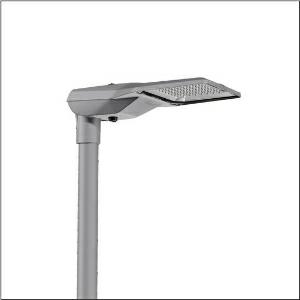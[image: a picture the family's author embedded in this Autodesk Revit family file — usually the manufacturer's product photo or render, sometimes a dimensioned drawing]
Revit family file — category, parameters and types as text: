
# Revit family: streetlight_sl_21_midi___st1_0a_5xe3d63t08lb_b124
name_source: partatom
category: Lighting Fixtures
units: mm (PartAtom-declared; Revit-internal decimal feet)

## family parameters
Cut with Voids When Loaded = No
Host = Face
Light Source = No
Part Type = Normal
Room Calculation Point = No
Round Connector Dimension = Use Diameter
Shared = No

## types (1)
- --- (1 x LED, 12860 lm, 99.6 W, 2700K)
    Apparent Load = 100 VA
    CIE Flux Codes = 37 72 97 100 100
    Color Rendering = 70
    Color Temperature = 2700K
    Default Elevation = 1800 mm
    Description = Streetlight SL 21 midi, mast luminaire, primary light control with lens, of PMMA, primary optical cover: cover, of toughened safety glass, transparent, light distribution: ST1.0a, light emission: direct distribution, primary light characteristic: asymmetric, installation type: side-entry, post-top, LED, High Power LED, rated luminous flux: 12.860lm, luminous efficacy: 129lm/W, light colour: 727, colour temperature: 2700K, control gear: D4i, control: overheat protection, constant luminous flux control, time-dependent luminous flux control, flexible luminous flux parameterisation, pre-setting: logarithmic dimming characteristic, mains connection: 230..240V, AC, 50/60Hz, start of lifetime: 100W, end of service life: 102W, reduction: 45W, luminaire housing, of diecast aluminium, powder-coated, SITECO metallic grey (DB 702S), corrosivity category C5 high according to DIN EN ISO 12944, please order mast flange separately, inclination adjustable: 0°, 5°, 10°, 15°, sealing non-destructively replaceable, multi-level sealing system, length: 644mm, width: 335mm, height: 110mm, mast flange for spigot size: 42mm (side-entry): 5XC10008XM4, 60/48mm (side-entry/post-top): 5XC10108XM2, 76/60mm (side-entry/post-top): 5XC10108XM1, mounting height: 4..8m, Smart Interface below and above, protection rating (complete): IP66, insulation class (complete): insulation class II (safety insulation), certification: CE, ENEC, ENEC+, VDE, impact resistance: IK10, permissible operating ambient temperature for outdoor applications: -40..+50°C, standard-compliant lighting for roads and squares, packaging unit: 1 piece

Light Distribution: ST1.0a
    Height = 111 mm
    Lamp = 1 x LED
    Lamp Light Flux = 12860 lm
    Lamp Power = 99.6 W
    Lamp count = 1
    Length = 644 mm
    Luminous efficacy = 129 lm/W
    Manufacturer = Siteco
    ModVariant = No
    Model = 5XE3D63T08LB
    Number of Poles = 1
    OnlyDefault = Yes
    Power Factor = 1
    Product Name = Streetlight SL 21 midi | ST1.0a
    Product group = mast luminaire | pylon top
    ProductGroupID = 6100
    Protection Class = Protection class II
    Protection Degree = IP 66
    RLX_Detail_Level = 1
    RLX_Emergency_Light_Flux = 0 lm
    RLX_Emergency_Type = 0
    RLX_Emergency_Type_DB = No
    RlxData = <blob elided: 26973 chars, md5=e7eaf4b6>
    Socket = socket
    Standby Power = 0 W
    System Light Flux = 12860 lm
    System Power = 100 W
    Type Comments = factory setting: luminous flux: 100 % | dim-lin: 254 | 1020 mA
    Type Image = l_1004304.jpg
    URL = http://relux.com
    VarID = @adj_031729
    Voltage = 0 V
    Weight = 0.00 kg
    Width = 336 mm

## geometry (parser evidence)
native form markers: Blend x4, Sweep x10
no freeform markers — native parametric forms only
